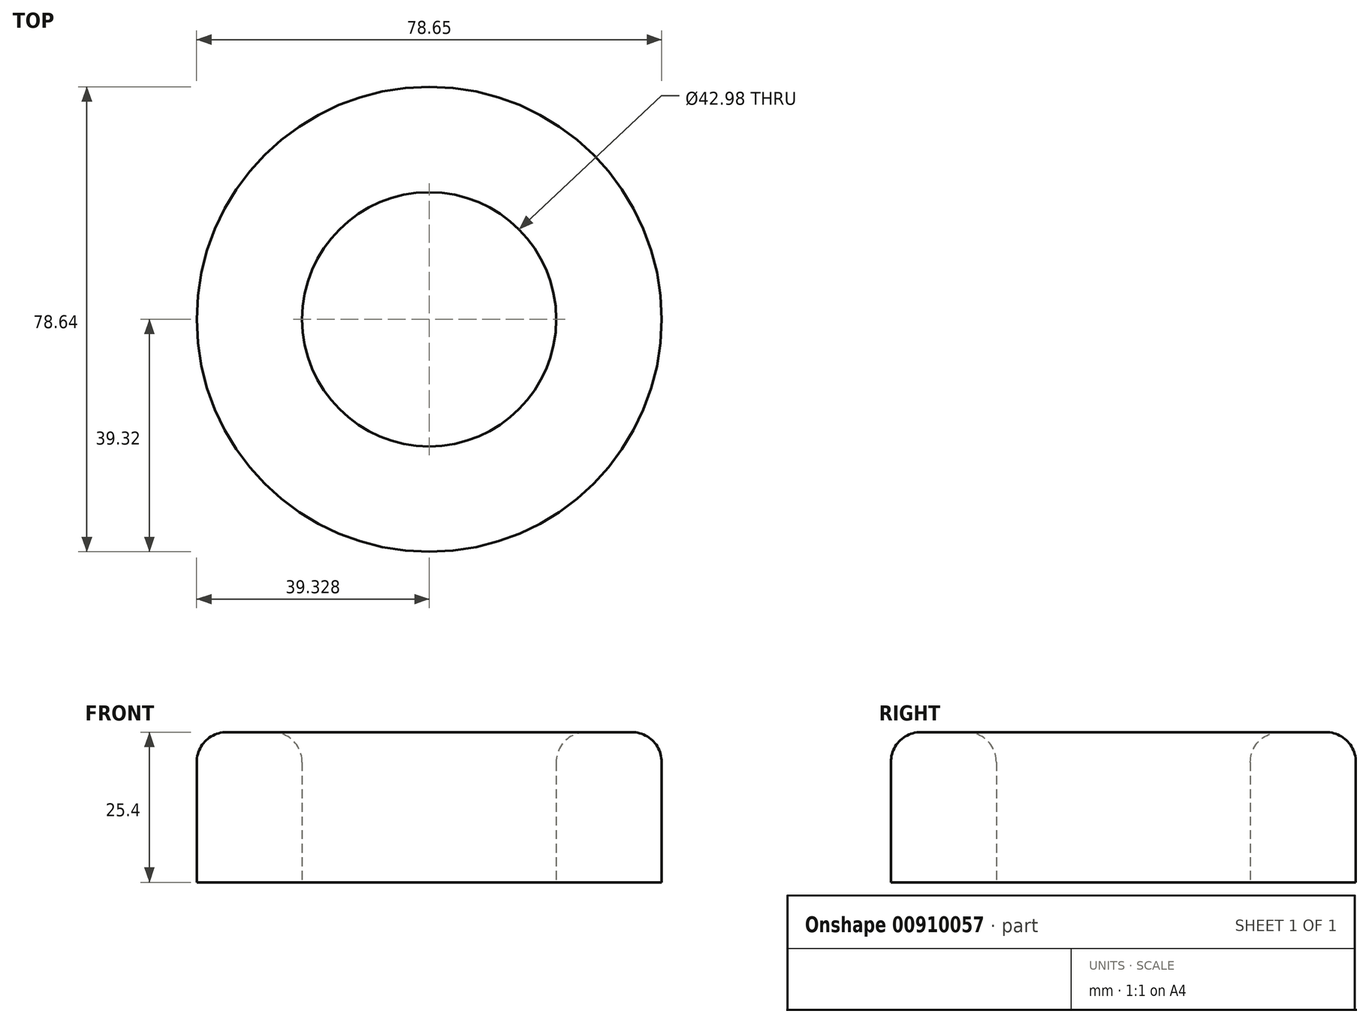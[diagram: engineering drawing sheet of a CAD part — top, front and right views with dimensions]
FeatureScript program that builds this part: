
annotation { "Feature Type Name" : "Feature", "Feature Type Description" : "" }
export const myFeature = defineFeature(function(context is Context, id is Id, definition is map)
    precondition{}
    {
        {
            var Q0;
            Q0=qCreatedBy(makeId("Top.planeOp"),FACE);
            var sketch = newSketch(context, id + "F0", { "sketchPlane" : qUnion([Q0])});
            skCircle(sketch, "E0", {"center": v(3.72, 0) * mm, "radius": 39.32 * mm});
            skCircle(sketch, "E1", {"center": v(3.72, 0) * mm, "radius": 21.5 * mm});
            skSolve(sketch);
        }
        {
            var Q0;
            Q0 = qSketchRegion(id + "F0", true);
            extrude(context, id + "F1", {"entities" : qUnion([Q0]), "depth" : 18.29 * mm, "offsetDistance" : 25.4 * mm});
        }
        {
            var Q0;
            Q0 = qSketchRegion(id + "F0", true);
            extrude(context, id + "F2", {"entities" : qUnion([Q0]), "operationType" : NewBodyOperationType.ADD, "depth" : 25.4 * mm, "offsetDistance" : 25.4 * mm});
        }
        {
            var Q0;
            Q0=makeQuery(id+"F2.opExtrude","CAP_FACE",FACE,{"disambiguationData":[OSD([sQuery(id+"F0.wireOp",EDGE,"E0"),sQuery(id+"F0.wireOp",EDGE,"E1")])],"isStart":false});
            fillet(context, id + "F3", {"entities" : qUnion([Q0]), "radius" : 5.08 * mm, "tangentPropagation" : true, "allowEdgeOverflow" : false});
        }
    });
